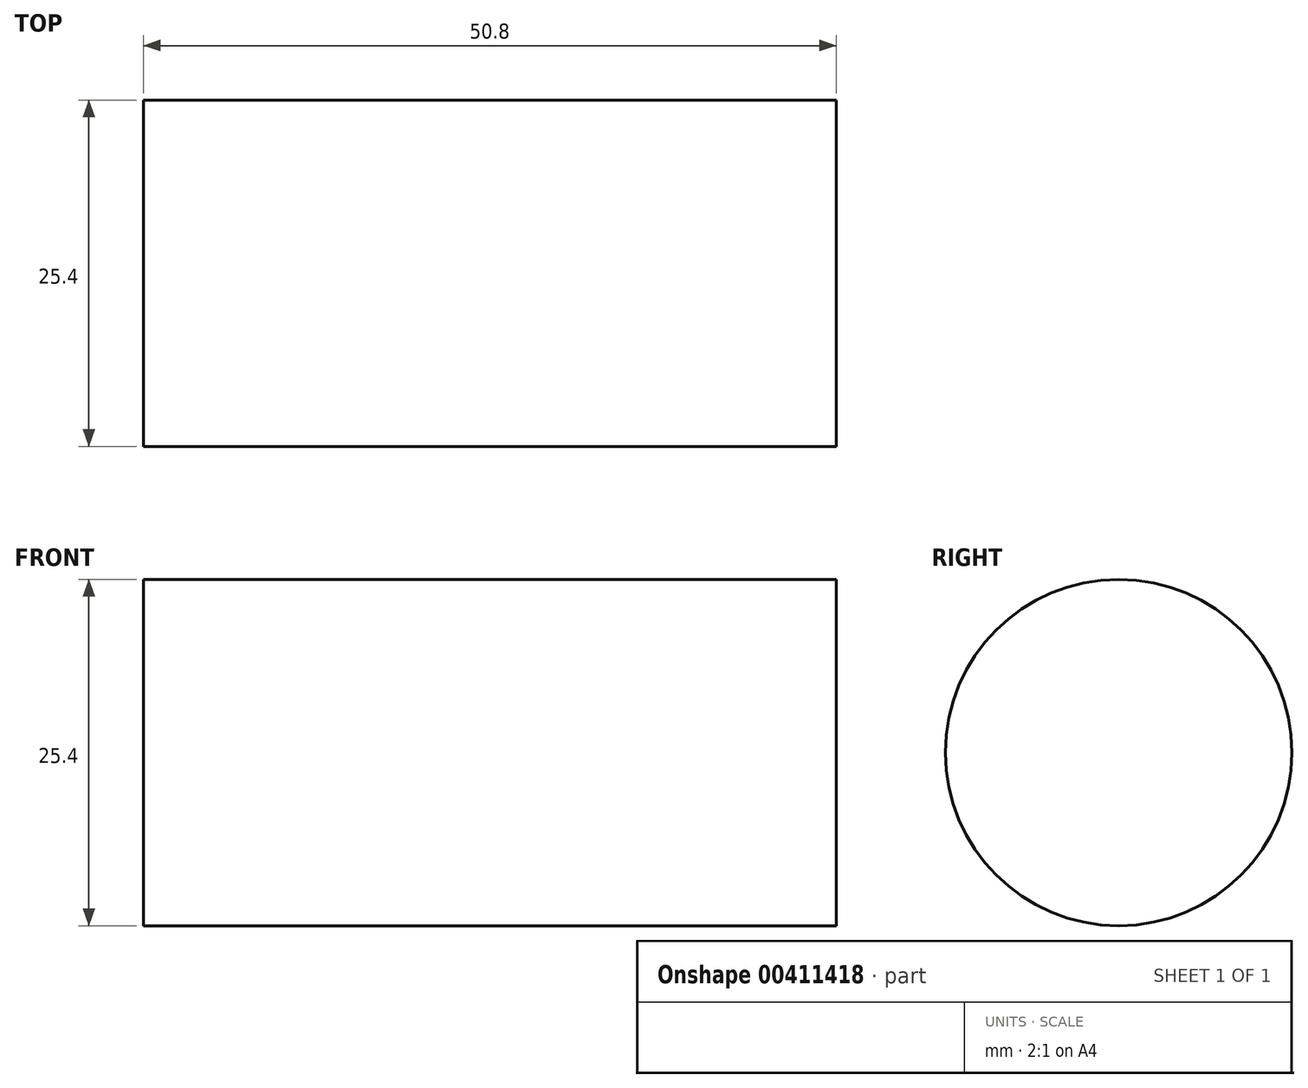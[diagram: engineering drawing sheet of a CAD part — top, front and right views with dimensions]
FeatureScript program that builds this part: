
annotation { "Feature Type Name" : "Feature", "Feature Type Description" : "" }
export const myFeature = defineFeature(function(context is Context, id is Id, definition is map)
    precondition{}
    {
        {
            var Q0;
            Q0=qCreatedBy(makeId("Right.planeOp"),FACE);
            var sketch = newSketch(context, id + "F0", { "sketchPlane" : qUnion([Q0])});
            skCircle(sketch, "E0", {"center": v(0, 11.09) * mm, "radius": 12.7 * mm});
            skSolve(sketch);
        }
        {
            var Q0;
            Q0=makeQuery(id+"F0.imprint","IMPRINT",FACE,{"disambiguationData":[TD([[makeQuery(id+"F0.imprint","IMPRINT",EDGE,{"derivedFrom":sQuery(id+"F0.wireOp",EDGE,"E0")}),1.0]])]});
            extrude(context, id + "F1", {"entities" : qUnion([Q0]), "depth" : 50.8 * mm});
        }
    });
